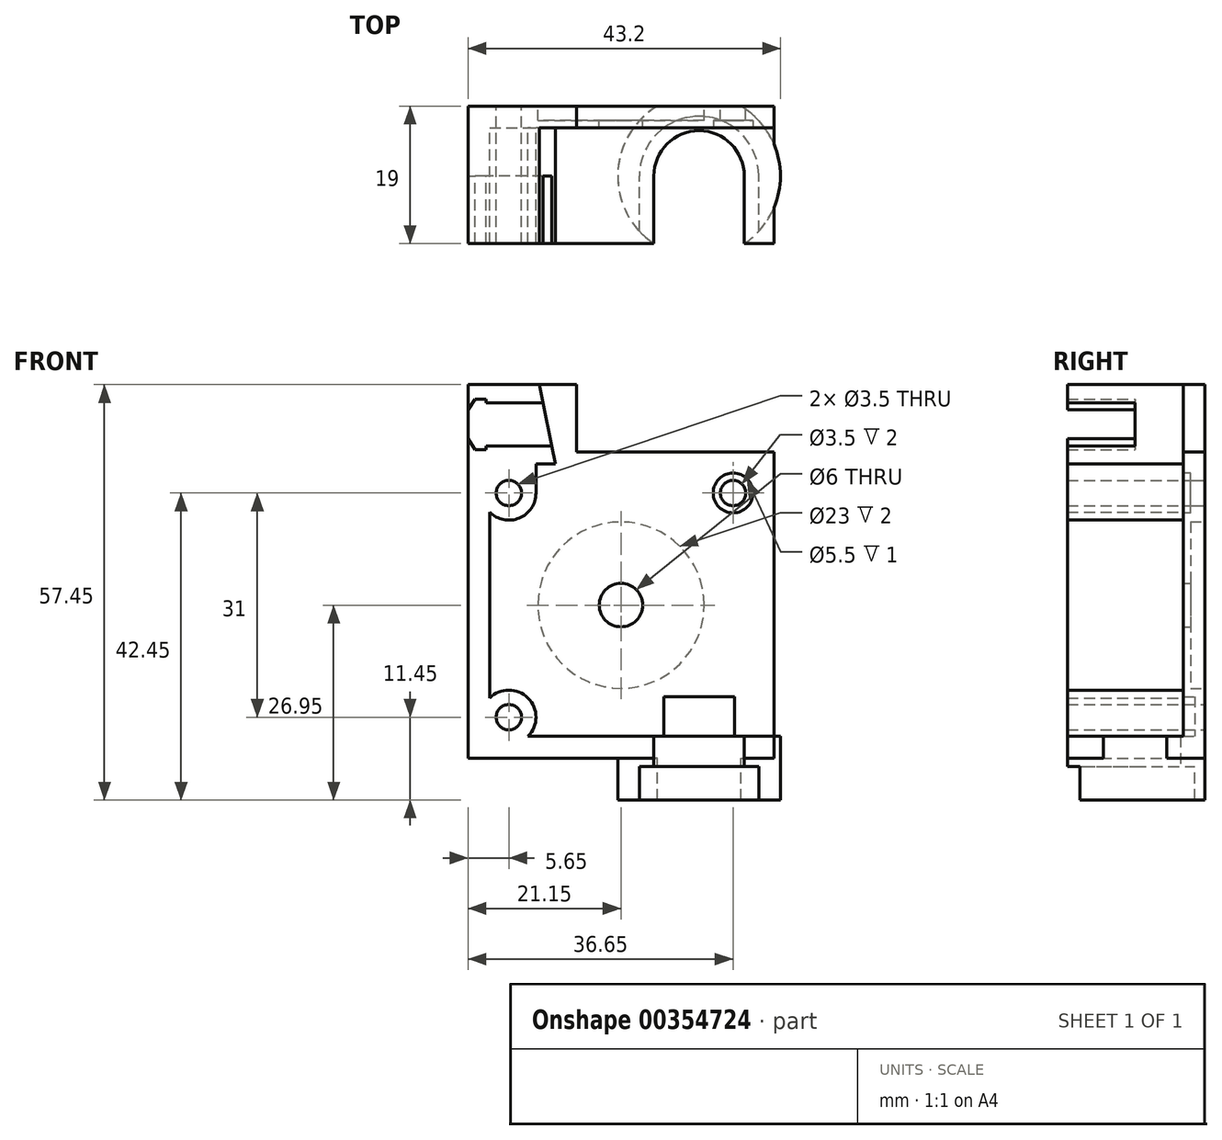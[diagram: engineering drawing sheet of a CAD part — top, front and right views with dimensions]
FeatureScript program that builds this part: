
annotation { "Feature Type Name" : "Feature", "Feature Type Description" : "" }
export const myFeature = defineFeature(function(context is Context, id is Id, definition is map)
    precondition{}
    {
        {
            var Q0;
            Q0=qCreatedBy(makeId("Front.planeOp"),FACE);
            var sketch = newSketch(context, id + "F0", { "sketchPlane" : qUnion([Q0])});
            skLineSegment(sketch, "E0.bottom", {"start": v(21.15, 21.15) * mm, "end": v(-21.15, 21.15) * mm});
            skLineSegment(sketch, "E0.top", {"start": v(21.15, -21.15) * mm, "end": v(-21.15, -21.15) * mm});
            skLineSegment(sketch, "E0.left", {"start": v(21.15, 21.15) * mm, "end": v(21.15, -21.15) * mm});
            skLineSegment(sketch, "E0.right", {"start": v(-21.15, 21.15) * mm, "end": v(-21.15, -21.15) * mm});
            skPoint(sketch, "E0.middle", {"position": v(0, 0) * mm});
            skCircle(sketch, "E1", {"center": v(-15.5, 15.5) * mm, "radius": 1.75 * mm});
            skCircle(sketch, "E2.MirrorC", {"center": v(15.5, 15.5) * mm, "radius": 1.75 * mm});
            skCircle(sketch, "E3.MirrorC", {"center": v(-15.5, -15.5) * mm, "radius": 1.75 * mm});
            skCircle(sketch, "E4.MirrorC", {"center": v(15.5, -15.5) * mm, "radius": 1.75 * mm, "construction": true});
            skCircle(sketch, "E5", {"center": v(0, 0) * mm, "radius": 3 * mm});
            skSolve(sketch);
        }
        {
            var Q0;
            Q0=qSketchRegion(id+"F0",true);
            extrude(context, id + "F1", {"entities" : qUnion([Q0]), "depth" : 3 * mm});
        }
        {
            var Q0;
            Q0=makeQuery(id+"F1.opExtrude","CAP_FACE",FACE,{"disambiguationData":[OSD([sQuery(id+"F0.wireOp",EDGE,"E0.bottom"),sQuery(id+"F0.wireOp",EDGE,"E0.top"),sQuery(id+"F0.wireOp",EDGE,"E0.left"),sQuery(id+"F0.wireOp",EDGE,"E0.right"),sQuery(id+"F0.wireOp",EDGE,"E1"),sQuery(id+"F0.wireOp",EDGE,"E2.MirrorC"),sQuery(id+"F0.wireOp",EDGE,"E3.MirrorC"),sQuery(id+"F0.wireOp",EDGE,"E4.MirrorC"),sQuery(id+"F0.wireOp",EDGE,"E5")])],"isStart":true});
            var sketch = newSketch(context, id + "F2", { "sketchPlane" : qUnion([Q0])});
            skCircle(sketch, "E6", {"center": v(0, 0) * mm, "radius": 11.5 * mm});
            skSolve(sketch);
        }
        {
            var Q0;
            Q0=qSketchRegion(id+"F2",true);
            extrude(context, id + "F3", {"entities" : qUnion([Q0]), "operationType" : NewBodyOperationType.REMOVE, "oppositeDirection" : true, "depth" : 2 * mm});
        }
        {
            var Q0;
            Q0=makeQuery(id+"F1.opExtrude","CAP_FACE",FACE,{"disambiguationData":[OSD([sQuery(id+"F0.wireOp",EDGE,"E0.bottom"),sQuery(id+"F0.wireOp",EDGE,"E0.top"),sQuery(id+"F0.wireOp",EDGE,"E0.left"),sQuery(id+"F0.wireOp",EDGE,"E0.right"),sQuery(id+"F0.wireOp",EDGE,"E1"),sQuery(id+"F0.wireOp",EDGE,"E2.MirrorC"),sQuery(id+"F0.wireOp",EDGE,"E3.MirrorC"),sQuery(id+"F0.wireOp",EDGE,"E4.MirrorC"),sQuery(id+"F0.wireOp",EDGE,"E5")])],"isStart":false});
            var sketch = newSketch(context, id + "F4", { "sketchPlane" : qUnion([Q0])});
            skLineSegment(sketch, "E7", {"start": v(-21.15, 21.15) * mm, "end": v(-11.75, 21.15) * mm});
            skLineSegment(sketch, "E8.MirrorCS", {"start": v(-11.75, 15.5) * mm, "end": v(-11.75, 21.15) * mm});
            skCircle(sketch, "E9.0", {"center": v(-15.5, 15.5) * mm, "radius": 1.75 * mm});
            skCircle(sketch, "E9.1", {"center": v(15.5, 15.5) * mm, "radius": 1.75 * mm});
            skCircle(sketch, "E9.3", {"center": v(-15.5, -15.5) * mm, "radius": 1.75 * mm});
            skArc(sketch, "E10", {"start": v(-18.15, 12.85) * mm, "mid": v(-14.06, 12.04) * mm, "end": v(-11.75, 15.5) * mm});
            skArc(sketch, "E11.MirrorC", {"start": v(-18.15, -12.85) * mm, "mid": v(-12.85, -12.85) * mm, "end": v(-12.85, -18.15) * mm});
            skLineSegment(sketch, "E12.0", {"start": v(21.15, -21.15) * mm, "end": v(-21.15, -21.15) * mm});
            skLineSegment(sketch, "E13.trimOffspring", {"start": v(-18.15, 12.85) * mm, "end": v(-18.15, -12.85) * mm});
            skLineSegment(sketch, "E14.trimOffspring", {"start": v(21.15, -18.15) * mm, "end": v(-12.85, -18.15) * mm});
            skLineSegment(sketch, "E15", {"start": v(21.15, -18.15) * mm, "end": v(21.15, -21.15) * mm});
            skLineSegment(sketch, "E16.trimOffspring", {"start": v(-21.15, 21.15) * mm, "end": v(-21.15, -21.15) * mm});
            skLineSegment(sketch, "E17", {"start": v(-11.75, 15.5) * mm, "end": v(-11.75, 15.5) * mm});
            skSolve(sketch);
        }
        {
            var Q0;
            Q0=makeQuery(id+"F4.imprint","IMPRINT",FACE,{"disambiguationData":[TD([[makeQuery(id+"F4.imprint","IMPRINT",EDGE,{"derivedFrom":sQuery(id+"F4.wireOp",EDGE,"E7")}),1.0]])]});
            extrude(context, id + "F5", {"entities" : qUnion([Q0]), "operationType" : NewBodyOperationType.ADD, "depth" : 16 * mm});
        }
        {
            var Q0;
            Q0=qCreatedBy(makeId("Front.planeOp"),FACE);
            cPlane(context, id + "F6", {"entities" : qUnion([Q0]), "cplaneType" : CPlaneType.OFFSET, "offset" : (7.65 + 2) * mm, "width" : 150 * mm, "height" : 150 * mm});
        }
        {
            var Q0;
            Q0=qCreatedBy(id+"F6.planeOp",FACE);
            var sketch = newSketch(context, id + "F7", { "sketchPlane" : qUnion([Q0])});
            skCircle(sketch, "E18", {"center": v(0, 0) * mm, "radius": 6 * mm, "construction": true});
            skCircle(sketch, "E19", {"center": v(15.5, 15.5) * mm, "radius": 15.92 * mm, "construction": true});
            skCircle(sketch, "E20", {"center": v(15.5, 15.5) * mm, "radius": 4.5 * mm, "construction": true});
            skCircle(sketch, "E21", {"center": v(15.5, 15.5) * mm, "radius": 3.75 * mm, "construction": true});
            skLineSegment(sketch, "E22.1", {"start": v(10.8, 32.66) * mm, "end": v(10.8, -28.23) * mm, "construction": true});
            skSolve(sketch);
        }
        {
            var Q0;
            Q0=qCreatedBy(id+"F6.planeOp",FACE);
            var sketch = newSketch(context, id + "F8", { "sketchPlane" : qUnion([Q0])});
            skLineSegment(sketch, "E23", {"start": v(-29.91, 25) * mm, "end": v(26.14, 25) * mm, "construction": true});
            skLineSegment(sketch, "E24", {"start": v(0, 28) * mm, "end": v(-18.65, 28) * mm});
            skLineSegment(sketch, "E25.MirrorCS", {"start": v(0, 22) * mm, "end": v(-18.65, 22) * mm});
            skLineSegment(sketch, "E26.left", {"start": v(-18.65, 28.5) * mm, "end": v(-18.65, 28) * mm});
            skLineSegment(sketch, "E27.trimOffspring", {"start": v(-18.65, 28.5) * mm, "end": v(-20.15, 28.5) * mm});
            skLineSegment(sketch, "E28.MirrorCS", {"start": v(-18.65, 21.5) * mm, "end": v(-18.65, 22) * mm});
            skLineSegment(sketch, "E29.trimOffspring", {"start": v(-18.65, 21.5) * mm, "end": v(-20.15, 21.5) * mm});
            skLineSegment(sketch, "E30", {"start": v(-21.15, 27) * mm, "end": v(-21.15, 23) * mm});
            skLineSegment(sketch, "E31", {"start": v(0, 28) * mm, "end": v(0, 22) * mm});
            skLineSegment(sketch, "E32", {"start": v(-21.15, 27) * mm, "end": v(-20.15, 28.5) * mm});
            skLineSegment(sketch, "E33.MirrorCS", {"start": v(-21.15, 23) * mm, "end": v(-20.15, 21.5) * mm});
            skSolve(sketch);
        }
        {
            var Q0;
            Q0=qCreatedBy(makeId("Front.planeOp"),FACE);
            var sketch = newSketch(context, id + "F9", { "sketchPlane" : qUnion([Q0])});
            skLineSegment(sketch, "E34.left", {"start": v(-21.15, 19.5) * mm, "end": v(-21.15, 30.5) * mm});
            skLineSegment(sketch, "E34.right", {"start": v(-6.15, 19.5) * mm, "end": v(-6.15, 30.5) * mm});
            skLineSegment(sketch, "E35.MirrorCS", {"start": v(-21.15, 30.5) * mm, "end": v(-6.15, 30.5) * mm});
            skCircle(sketch, "E36.0", {"center": v(-15.5, 15.5) * mm, "radius": 1.75 * mm});
            skLineSegment(sketch, "E37.trimOffspring", {"start": v(-21.15, 19.5) * mm, "end": v(-6.15, 19.5) * mm});
            skSolve(sketch);
        }
        {
            var Q0;
            {var subQ0=sQuery(id+"F9.wireOp",EDGE,"E34.top");Q0=makeQuery(id+"F9.imprint","IMPRINT",FACE,{"disambiguationData":[TD([[makeQuery(id+"F9.imprint","IMPRINT",EDGE,{"derivedFrom":subQ0}),-1.0]])]});}
            var Q1;
            Q1=makeQuery(id+"F9.imprint","IMPRINT",FACE,{"disambiguationData":[TD([[makeQuery(id+"F9.imprint","IMPRINT",EDGE,{"derivedFrom":sQuery(id+"F9.wireOp",EDGE,"E34.left")}),-1.0]])]});
            var Q2;
            Q2=makeQuery(id+"F5.opExtrude","CAP_FACE",FACE,{"disambiguationData":[OSD([sQuery(id+"F4.wireOp",EDGE,"E7"),sQuery(id+"F4.wireOp",EDGE,"E8.MirrorCS"),sQuery(id+"F4.wireOp",EDGE,"E9.0"),sQuery(id+"F4.wireOp",EDGE,"E9.3"),sQuery(id+"F4.wireOp",EDGE,"E10"),sQuery(id+"F4.wireOp",EDGE,"E11.MirrorC"),sQuery(id+"F4.wireOp",EDGE,"E12.0"),sQuery(id+"F4.wireOp",EDGE,"E13.trimOffspring"),sQuery(id+"F4.wireOp",EDGE,"E14.trimOffspring"),sQuery(id+"F4.wireOp",EDGE,"E15"),sQuery(id+"F4.wireOp",EDGE,"E16.trimOffspring")])],"isStart":false});
            extrude(context, id + "F10", {"entities" : qUnion([Q0, Q1]), "operationType" : NewBodyOperationType.ADD, "endBound" : BoundingType.UP_TO_SURFACE, "endBoundEntityFace" : qUnion([Q2]), "depth" : 25 * mm});
        }
        {
            var Q0;
            Q0=qSketchRegion(id+"F8",true);
            extrude(context, id + "F11", {"entities" : qUnion([Q0]), "operationType" : NewBodyOperationType.REMOVE, "depth" : 10 * mm});
        }
        {
            var Q0;
            Q0=qCreatedBy(id+"F6.planeOp",FACE);
            var sketch = newSketch(context, id + "F12", { "sketchPlane" : qUnion([Q0])});
            skLineSegment(sketch, "E38.0", {"start": v(10.8, 32.15) * mm, "end": v(10.8, -42.47) * mm, "construction": true});
            skLineSegment(sketch, "E39.bottom", {"start": v(19.05, -18.15) * mm, "end": v(17.05, -18.15) * mm, "construction": true});
            skLineSegment(sketch, "E39.top", {"start": v(19.05, -12.65) * mm, "end": v(2.55, -12.65) * mm, "construction": true});
            skLineSegment(sketch, "E39.left", {"start": v(19.05, -18.15) * mm, "end": v(19.05, -12.65) * mm, "construction": true});
            skLineSegment(sketch, "E39.right", {"start": v(2.55, -18.15) * mm, "end": v(2.55, -12.65) * mm, "construction": true});
            skPoint(sketch, "E39.middle", {"position": v(10.8, -15.4) * mm});
            skLineSegment(sketch, "E40.top", {"start": v(17.05, -22.35) * mm, "end": v(4.55, -22.35) * mm, "construction": true});
            skLineSegment(sketch, "E40.left", {"start": v(17.05, -18.15) * mm, "end": v(17.05, -22.35) * mm, "construction": true});
            skLineSegment(sketch, "E40.right", {"start": v(4.55, -18.15) * mm, "end": v(4.55, -22.35) * mm, "construction": true});
            skPoint(sketch, "E40.middle", {"position": v(10.8, -20.25) * mm});
            skLineSegment(sketch, "E41.bottom", {"start": v(19.05, -22.35) * mm, "end": v(17.05, -22.35) * mm, "construction": true});
            skLineSegment(sketch, "E41.top", {"start": v(19.05, -26.95) * mm, "end": v(2.55, -26.95) * mm, "construction": true});
            skLineSegment(sketch, "E41.left", {"start": v(19.05, -22.35) * mm, "end": v(19.05, -26.95) * mm, "construction": true});
            skLineSegment(sketch, "E41.right", {"start": v(2.55, -22.35) * mm, "end": v(2.55, -26.95) * mm, "construction": true});
            skPoint(sketch, "E41.middle", {"position": v(10.8, -24.65) * mm});
            skLineSegment(sketch, "E42.trimOffspring", {"start": v(4.55, -18.15) * mm, "end": v(2.55, -18.15) * mm, "construction": true});
            skLineSegment(sketch, "E43.trimOffspring", {"start": v(4.55, -22.35) * mm, "end": v(2.55, -22.35) * mm, "construction": true});
            skPoint(sketch, "E44", {"position": v(10.8, -5.16) * mm});
            skSolve(sketch);
        }
        {
            var Q0;
            Q0=qCreatedBy(id+"F6.planeOp",FACE);
            var sketch = newSketch(context, id + "F13", { "sketchPlane" : qUnion([Q0])});
            skLineSegment(sketch, "E45.0", {"start": v(19.05, -18.15) * mm, "end": v(19.05, -12.65) * mm});
            skLineSegment(sketch, "E45.1", {"start": v(19.05, -18.15) * mm, "end": v(17.05, -18.15) * mm});
            skLineSegment(sketch, "E45.2", {"start": v(17.05, -18.15) * mm, "end": v(17.05, -22.35) * mm});
            skLineSegment(sketch, "E45.3", {"start": v(19.05, -22.35) * mm, "end": v(17.05, -22.35) * mm});
            skLineSegment(sketch, "E45.4", {"start": v(19.05, -22.35) * mm, "end": v(19.05, -26.95) * mm});
            skLineSegment(sketch, "E46", {"start": v(19.05, -12.65) * mm, "end": v(10.8, -12.65) * mm});
            skLineSegment(sketch, "E47", {"start": v(10.8, -12.65) * mm, "end": v(10.8, -26.95) * mm});
            skLineSegment(sketch, "E48", {"start": v(10.8, -26.95) * mm, "end": v(19.05, -26.95) * mm});
            skSolve(sketch);
        }
        {
            var Q0;
            Q0=qSketchRegion(id+"F13",true);
            var Q1;
            Q1=sQuery(id+"F12.wireOp",EDGE,"E38.0");
            revolve(context, id + "F14", {"operationType" : NewBodyOperationType.REMOVE, "entities" : qUnion([Q0]), "axis" : qUnion([Q1]), "revolveType" : RevolveType.FULL, "oppositeDirection" : true});
        }
        {
            var Q0;
            Q0=qCreatedBy(id+"F6.planeOp",FACE);
            var sketch = newSketch(context, id + "F15", { "sketchPlane" : qUnion([Q0])});
            skLineSegment(sketch, "E49", {"start": v(8.3, 45.28) * mm, "end": v(8.3, -57.7) * mm, "construction": true});
            skLineSegment(sketch, "E50", {"start": v(13.3, -58.45) * mm, "end": v(13.3, 44.53) * mm, "construction": true});
            skLineSegment(sketch, "E51", {"start": v(8.3, -6.21) * mm, "end": v(13.3, -6.21) * mm, "construction": true});
            skPoint(sketch, "E52", {"position": v(10.8, -6.21) * mm});
            skLineSegment(sketch, "E53.0", {"start": v(2.55, -18.15) * mm, "end": v(2.55, -12.65) * mm, "construction": true});
            skLineSegment(sketch, "E53.1", {"start": v(4.55, -18.15) * mm, "end": v(2.55, -18.15) * mm, "construction": true});
            skLineSegment(sketch, "E53.2", {"start": v(4.55, -18.15) * mm, "end": v(4.55, -22.35) * mm, "construction": true});
            skLineSegment(sketch, "E53.3", {"start": v(4.55, -22.35) * mm, "end": v(2.55, -22.35) * mm, "construction": true});
            skLineSegment(sketch, "E53.4", {"start": v(2.55, -22.35) * mm, "end": v(2.55, -26.95) * mm, "construction": true});
            skLineSegment(sketch, "E53.5", {"start": v(17.05, -18.15) * mm, "end": v(17.05, -22.35) * mm});
            skLineSegment(sketch, "E53.6", {"start": v(19.05, -22.35) * mm, "end": v(17.05, -22.35) * mm});
            skLineSegment(sketch, "E53.7", {"start": v(19.05, -18.15) * mm, "end": v(17.05, -18.15) * mm});
            skLineSegment(sketch, "E53.8", {"start": v(19.05, -18.15) * mm, "end": v(19.05, -18.15) * mm});
            skLineSegment(sketch, "E53.9", {"start": v(19.05, -22.35) * mm, "end": v(19.05, -26.95) * mm});
            skLineSegment(sketch, "E53.10", {"start": v(19.05, -26.95) * mm, "end": v(2.55, -26.95) * mm, "construction": true});
            skLineSegment(sketch, "E54.0", {"start": v(22.05, -18.15) * mm, "end": v(22.05, -26.95) * mm});
            skLineSegment(sketch, "E54.1", {"start": v(22.05, -29.95) * mm, "end": v(-0.45, -29.95) * mm, "construction": true});
            skLineSegment(sketch, "E54.2", {"start": v(-0.45, -21.15) * mm, "end": v(-0.45, -29.95) * mm, "construction": true});
            skLineSegment(sketch, "E55", {"start": v(19.05, -18.15) * mm, "end": v(22.05, -18.15) * mm});
            skLineSegment(sketch, "E56", {"start": v(19.05, -26.95) * mm, "end": v(22.05, -26.95) * mm});
            skLineSegment(sketch, "E57", {"start": v(22.05, -26.95) * mm, "end": v(22.05, -29.95) * mm, "construction": true});
            skSolve(sketch);
        }
        {
            var Q0;
            Q0=qSketchRegion(id+"F15",true);
            var Q1;
            Q1=sQuery(id+"F15.wireOp",EDGE,"E53.2");
            var Q2;
            Q2=sQuery(id+"F15.wireOp",EDGE,"E53.0");
            var Q3;
            Q3=sQuery(id+"F15.wireOp",EDGE,"E54.2");
            var Q4;
            Q4=sQuery(id+"F15.wireOp",EDGE,"E53.3");
            var Q5;
            Q5=sQuery(id+"F15.wireOp",EDGE,"E53.4");
            var Q6;
            Q6=sQuery(id+"F15.wireOp",EDGE,"E53.1");
            var Q7;
            Q7=sQuery(id+"F12.wireOp",EDGE,"E38.0");
            revolve(context, id + "F16", {"operationType" : NewBodyOperationType.ADD, "entities" : qUnion([Q0]), "surfaceEntities" : qUnion([Q1, Q2, Q3, Q4, Q5, Q6]), "axis" : qUnion([Q7]), "revolveType" : RevolveType.FULL});
        }
        {
            var Q0;
            Q0=qCreatedBy(id+"F6.planeOp",FACE);
            var sketch = newSketch(context, id + "F17", { "sketchPlane" : qUnion([Q0])});
            skLineSegment(sketch, "E58.0", {"start": v(2.55, -18.15) * mm, "end": v(2.55, -12.65) * mm});
            skLineSegment(sketch, "E58.1", {"start": v(19.05, -12.65) * mm, "end": v(2.55, -12.65) * mm});
            skLineSegment(sketch, "E58.2", {"start": v(19.05, -18.15) * mm, "end": v(19.05, -12.65) * mm});
            skLineSegment(sketch, "E58.3", {"start": v(17.05, -18.15) * mm, "end": v(17.05, -22.35) * mm});
            skLineSegment(sketch, "E58.4", {"start": v(4.55, -18.15) * mm, "end": v(4.55, -22.35) * mm});
            skLineSegment(sketch, "E58.5", {"start": v(4.55, -18.15) * mm, "end": v(2.55, -18.15) * mm});
            skLineSegment(sketch, "E58.6", {"start": v(19.05, -18.15) * mm, "end": v(17.05, -18.15) * mm});
            skLineSegment(sketch, "E58.7", {"start": v(19.05, -22.35) * mm, "end": v(17.05, -22.35) * mm});
            skLineSegment(sketch, "E58.8", {"start": v(19.05, -22.35) * mm, "end": v(19.05, -26.95) * mm});
            skLineSegment(sketch, "E58.9", {"start": v(4.55, -22.35) * mm, "end": v(2.55, -22.35) * mm});
            skLineSegment(sketch, "E58.10", {"start": v(2.55, -22.35) * mm, "end": v(2.55, -26.95) * mm});
            skLineSegment(sketch, "E58.11", {"start": v(19.05, -26.95) * mm, "end": v(2.55, -26.95) * mm});
            skSolve(sketch);
        }
        {
            var Q0;
            Q0=qSketchRegion(id+"F17",true);
            extrude(context, id + "F18", {"entities" : qUnion([Q0]), "operationType" : NewBodyOperationType.REMOVE, "endBound" : BoundingType.THROUGH_ALL, "depth" : 25 * mm});
        }
        {
            var Q0;
            Q0=qCreatedBy(makeId("Right.planeOp"),FACE);
            var sketch = newSketch(context, id + "F19", { "sketchPlane" : qUnion([Q0])});
            skLineSegment(sketch, "E59.bottom", {"start": v(0, 47.05) * mm, "end": v(28.32, 47.05) * mm});
            skLineSegment(sketch, "E59.top", {"start": v(0, -52.65) * mm, "end": v(28.32, -52.65) * mm});
            skLineSegment(sketch, "E59.left", {"start": v(0, 47.05) * mm, "end": v(0, -52.65) * mm});
            skLineSegment(sketch, "E59.right", {"start": v(28.32, 47.05) * mm, "end": v(28.32, -52.65) * mm});
            skSolve(sketch);
        }
        {
            var Q0;
            Q0=makeQuery(id+"F19.imprint","IMPRINT",FACE,{"disambiguationData":[TD([[makeQuery(id+"F19.imprint","IMPRINT",EDGE,{"derivedFrom":sQuery(id+"F19.wireOp",EDGE,"E59.bottom")}),-1.0]])]});
            extrude(context, id + "F20", {"entities" : qUnion([Q0]), "operationType" : NewBodyOperationType.REMOVE, "endBound" : BoundingType.THROUGH_ALL, "depth" : 25 * mm});
        }
        {
            var Q0;
            Q0=makeQuery(id+"F1.opExtrude","CAP_FACE",FACE,{"disambiguationData":[OSD([sQuery(id+"F0.wireOp",EDGE,"E0.bottom"),sQuery(id+"F0.wireOp",EDGE,"E0.top"),sQuery(id+"F0.wireOp",EDGE,"E0.left"),sQuery(id+"F0.wireOp",EDGE,"E0.right"),sQuery(id+"F0.wireOp",EDGE,"E1"),sQuery(id+"F0.wireOp",EDGE,"E2.MirrorC"),sQuery(id+"F0.wireOp",EDGE,"E3.MirrorC"),sQuery(id+"F0.wireOp",EDGE,"E5")])],"isStart":false});
            var sketch = newSketch(context, id + "F21", { "sketchPlane" : qUnion([Q0])});
            skArc(sketch, "E60", {"start": v(4.9, 1) * mm, "mid": v(1, -4.9) * mm, "end": v(-4.9, -1) * mm});
            skLineSegment(sketch, "E61", {"start": v(4.9, 1) * mm, "end": v(-4.02, 45.1) * mm});
            skLineSegment(sketch, "E62", {"start": v(-4.9, -1) * mm, "end": v(-13.82, 43.12) * mm});
            skArc(sketch, "E63", {"start": v(-13.82, 43.12) * mm, "mid": v(-9.91, 49) * mm, "end": v(-4.02, 45.1) * mm});
            skCircle(sketch, "E64", {"center": v(-0.23, 16.28) * mm, "radius": 8 * mm, "construction": true});
            skLineSegment(sketch, "E65", {"start": v(-8.92, 44.1) * mm, "end": v(0, 0) * mm, "construction": true});
            skCircle(sketch, "E66.0", {"center": v(15.5, 15.5) * mm, "radius": 3.75 * mm, "construction": true});
            skLineSegment(sketch, "E67", {"start": v(-0.23, 16.28) * mm, "end": v(-3.17, 15.68) * mm, "construction": true});
            skSolve(sketch);
        }
        {
            var Q0;
            Q0=qSketchRegion(id+"F21",true);
            extrude(context, id + "F22", {"entities" : qUnion([Q0]), "operationType" : NewBodyOperationType.REMOVE, "endBound" : BoundingType.THROUGH_ALL, "depth" : 25 * mm});
        }
        {
            var Q0;
            Q0=makeQuery(id+"F22.boolean.opBoolean","MERGE",FACE,{"derivedFrom":[makeQuery(id+"F1.opExtrude","CAP_FACE",FACE,{"disambiguationData":[OSD([sQuery(id+"F0.wireOp",EDGE,"E0.bottom"),sQuery(id+"F0.wireOp",EDGE,"E0.top"),sQuery(id+"F0.wireOp",EDGE,"E0.left"),sQuery(id+"F0.wireOp",EDGE,"E0.right"),sQuery(id+"F0.wireOp",EDGE,"E1"),sQuery(id+"F0.wireOp",EDGE,"E2.MirrorC"),sQuery(id+"F0.wireOp",EDGE,"E3.MirrorC"),sQuery(id+"F0.wireOp",EDGE,"E5")])],"isStart":false}),makeQuery(id+"F22.opExtrude","CAP_FACE",FACE,{"disambiguationData":[OSD([sQuery(id+"F21.wireOp",EDGE,"E60"),sQuery(id+"F21.wireOp",EDGE,"E61"),sQuery(id+"F21.wireOp",EDGE,"E62"),sQuery(id+"F21.wireOp",EDGE,"E63")])],"isStart":true})]});
            var sketch = newSketch(context, id + "F23", { "sketchPlane" : qUnion([Q0])});
            skCircle(sketch, "E68", {"center": v(15.5, 15.5) * mm, "radius": 2.75 * mm});
            skSolve(sketch);
        }
        {
            var Q0;
            Q0=makeQuery(id+"F23.imprint","IMPRINT",FACE,{"disambiguationData":[TD([[makeQuery(id+"F23.imprint","IMPRINT",EDGE,{"derivedFrom":sQuery(id+"F23.wireOp",EDGE,"E68")}),1.0]])]});
            extrude(context, id + "F24", {"entities" : qUnion([Q0]), "operationType" : NewBodyOperationType.REMOVE, "oppositeDirection" : true, "depth" : 1 * mm});
        }
    });
